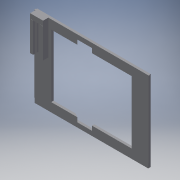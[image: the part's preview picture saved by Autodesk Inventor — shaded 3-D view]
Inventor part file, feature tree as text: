
AUTODESK INVENTOR PART (.ipt)
format: ipt  version: 2018.3 (Build 223284000, 284)  size: 240,640 bytes
history: native  units: mm
features: extrude x12, sketch x12, chamfer x2
ambient origin geometry x8: Origin, YZ Plane, XZ Plane, XY Plane, X Axis, Y Axis, Z Axis, Center Point
bodies: Solid1 (feature_tree)
feature tree (26):
  extrude  "Extrusion1"  Depth=2.8mm
  extrude  "Extrusion2"  Depth=0.7mm
  extrude  "Extrusion3"  Depth=0.7mm
  extrude  "Extrusion4"  Depth=85.0mm TaperAngle=0.0deg
  extrude  "Extrusion5"  Depth=5.42mm
  extrude  "Extrusion6"  Depth=0.6mm TaperAngle=0.0deg
  extrude  "Extrusion7"  Depth=1.25mm
  extrude  "Extrusion8"  Depth=33.0mm
  extrude  "Extrusion9"  Depth=2.0mm
  extrude  "Extrusion10"  Depth=6.0mm TaperAngle=0.0deg
  extrude  "Extrusion11"  Depth=2.0mm
  extrude  "Extrusion13"  Depth=33.0mm TaperAngle=0.0deg
  chamfer  "Chamfer1"  Distance=1.65mm
  chamfer  "Chamfer2"  Distance=1.6mm
  sketch  "Sketch1"  dims[d0=126.5mm d1=2.8mm]
  sketch  "Sketch2"  dims[d2=90.0mm d3=0.0mm d4=0.7mm]
  sketch  "Sketch3"  dims[d5=1.4mm d6=0.7mm]
  sketch  "Sketch4"  dims[d7=1.4mm d8=85.0mm d9=0.0mm]
  sketch  "Sketch5"  dims[d12=14.5mm d13=5.42mm]
  sketch  "Sketch6"  dims[d14=0.6mm d15=5.72mm d16=0.0mm]
  sketch  "Sketch7"  dims[d17=1.25mm d18=1.25mm]
  sketch  "Sketch8"  dims[d19=0.15mm d20=0.0mm d21=33.0mm]
  sketch  "Sketch9"  dims[d22=2.0mm d23=2.0mm]
  sketch  "Sketch10"  dims[d24=10.5mm d25=6.0mm d26=0.0mm]
  sketch  "Sketch11"  dims[d27=4.0mm d28=2.0mm]
  sketch  "Sketch12"  dims[d29=1.5mm d30=33.0mm d31=0.0mm d32=1.65mm d33=1.6mm d34=33.0mm d35=0.0mm d36=1.5mm d37=2.0mm d38=33.0mm d39=0.0mm d40=1.65mm d41=1.6mm d42=33.0mm d43=0.0mm d47=1.5mm d48=0.0mm d49=1.5mm d50=0.0mm d51=90.0mm d52=70.0mm d55=18.25mm d56=18.25mm d57=10.0mm d58=10.0mm d59=16.43mm d60=5.0mm d61=29.07mm d62=1.5mm d63=0.0mm d64=4.5mm d65=2.0mm d66=30.0deg d67=5.0mm d68=29.07mm d69=4.5mm d70=2.0mm d71=30.0deg]
